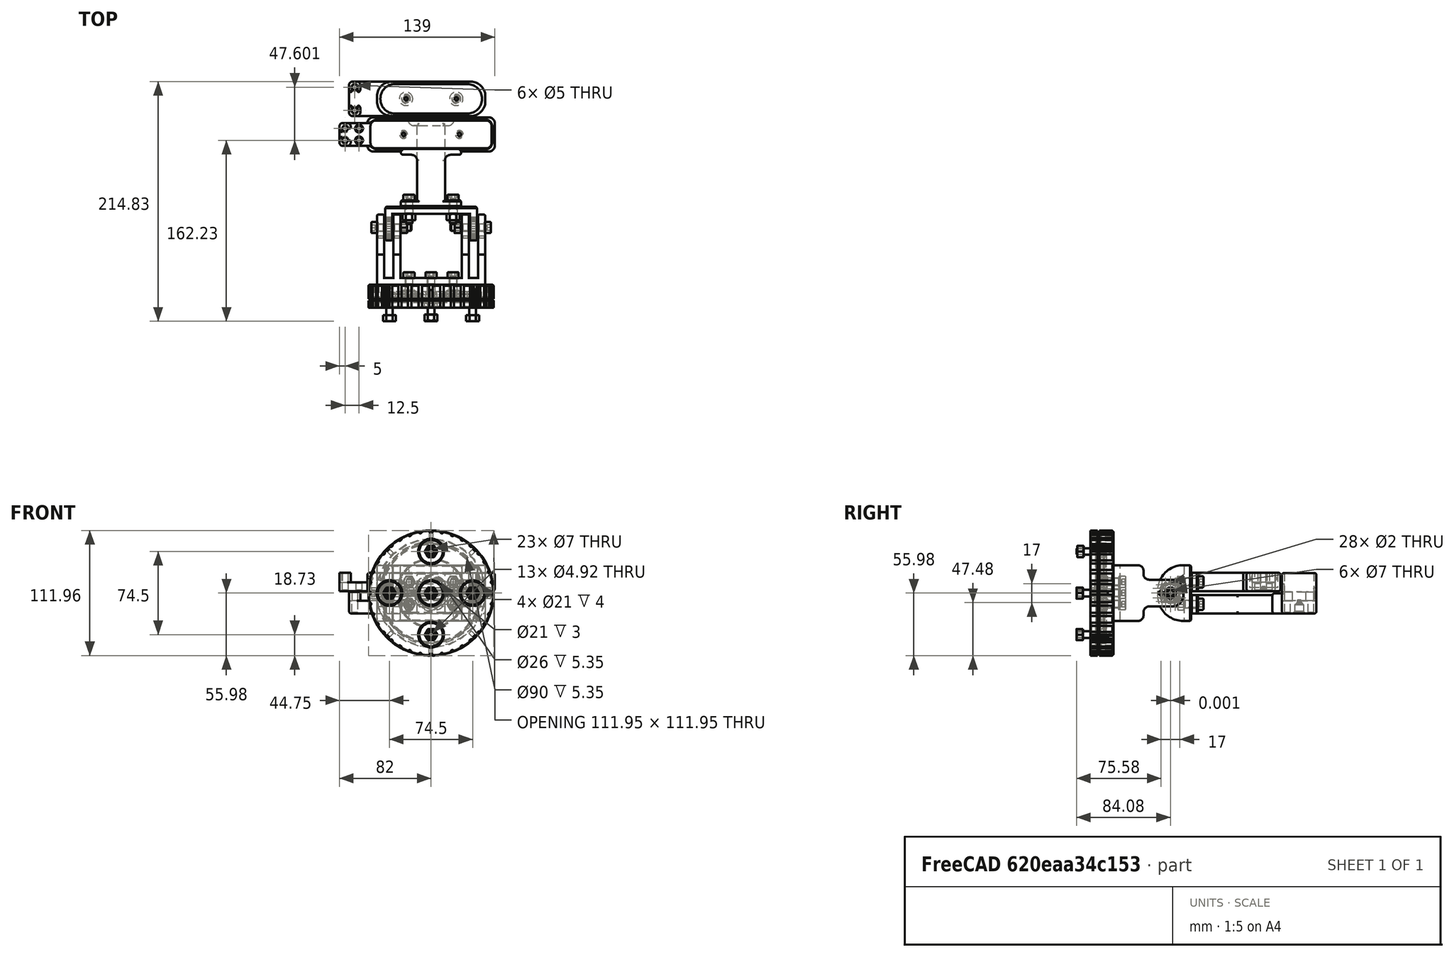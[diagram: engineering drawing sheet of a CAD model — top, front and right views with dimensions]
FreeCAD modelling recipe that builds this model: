
FCSTD DOCUMENT  (FreeCAD 0.18R15576 (Git))
Label: T265_D435i_Fixture
License: All rights reserved
LicenseURL: http://en.wikipedia.org/wiki/All_rights_reserved
objects: Part::FeaturePython×34, Part::Feature×6, App::DocumentObjectGroup×1
note: 40 computed .brp shape members not serialized (recipe doc carries the construction recipe); baked Part::Feature solids carry a one-line shape summary decoded from their .brp

FEATURE [Part::Feature] Chamfer003001002001003001001  label="az_top"
  Placement = pos=(0,-9,0) rot=(0,0,1;0rad)
  shape: bbox 112 x 12.7 x 116.8 mm, 171 faces (baked)
FEATURE [Part::Feature] Chamfer003001002001003001002004001002001001  label="az_bottom"
  Placement = pos=(0,-10,0) rot=(0,0,1;0rad)
  shape: bbox 112 x 14.62 x 116.8 mm, 201 faces (baked)
FEATURE [Part::Feature] Chamfer003001002001003001002004001002001002001  label="el_bottom"
  Placement = pos=(0,-3,0) rot=(0,0,1;0rad)
  shape: bbox 96.9 x 63.75 x 50.82 mm, 209 faces (baked)
FEATURE [Part::Feature] Chamfer003001002001003001002004001002001002002001  label="el_top"
  Placement = pos=(0,-6,0) rot=(0,0,1;0rad)
  shape: bbox 82.2 x 31.9 x 53.79 mm, 132 faces (baked)
FEATURE [Part::Feature] Chamfer003001002001003001002004001002001002002002001001  label="t265_fixture"
  shape: bbox 139.4 x 80.91 x 16.5 mm, 152 faces (baked)
FEATURE [Part::Feature] Chamfer003001002001003001002004001002001002002002001002001  label="d435i_fixture"
  shape: bbox 123.1 x 113.7 x 36.3 mm, 188 faces (baked)
FEATURE [Part::FeaturePython] Screw  label="M6x30-Screw001"  # Fasteners workbench fastener (typed FeaturePython)
  Placement = pos=(39.35,-83.399,-26.6996) rot=(0,1,0;1.5708rad)
  baseObject = -> Chamfer003001002001003001002004001002001002001 [Edge176]
  diameter = 7
  invert = true
  length = 7
  matchOuter = false
  offset = 0
  thread = false
  type = 15
FEATURE [Part::FeaturePython] Screw001  label="M6x30-Screw"  # Fasteners workbench fastener (typed FeaturePython)
  Placement = pos=(-55.55,-83.399,-26.6996) rot=(0,-1,0;1.5708rad)
  baseObject = -> Chamfer003001002001003001002004001002001002001 [Edge150]
  diameter = 7
  invert = false
  length = 7
  matchOuter = false
  offset = 0
  thread = false
  type = 15
FEATURE [Part::FeaturePython] Nut001  label="M6-Nut003"  # Fasteners workbench fastener (typed FeaturePython)
  Placement = pos=(-29.55,-83.399,-26.6996) rot=(0,-1,0;1.5708rad)
  baseObject = -> Screw001 [Edge16]
  diameter = 2
  invert = false
  matchOuter = false
  offset = 4
  thread = false
  type = 5
FEATURE [Part::FeaturePython] Screw002  label="M6x20-Screw"  # Fasteners workbench fastener (typed FeaturePython)
  Placement = pos=(11.65,-59.9,-36.7) rot=(-1,0,0;1.5708rad)
  baseObject = -> Chamfer003001002001003001002004001002001002002002001002001 [Edge302]
  diameter = 7
  invert = false
  length = 5
  matchOuter = false
  offset = 0
  thread = false
  type = 15
FEATURE [Part::FeaturePython] Nut002  label="M6-Nut002"  # Fasteners workbench fastener (typed FeaturePython)
  Placement = pos=(11.65,-76.9,-36.7) rot=(-1,0,0;1.5708rad)
  baseObject = -> Screw002 [Edge14]
  diameter = 2
  invert = false
  matchOuter = false
  offset = 3
  thread = false
  type = 5
FEATURE [Part::FeaturePython] Screw003  label="M6x20-Screw001"  # Fasteners workbench fastener (typed FeaturePython)
  Placement = pos=(-27.85,-59.9,-36.7) rot=(-1,0,0;1.5708rad)
  baseObject = -> Chamfer003001002001003001002004001002001002002002001002001 [Edge63]
  diameter = 7
  invert = false
  length = 5
  matchOuter = false
  offset = 0
  thread = false
  type = 15
FEATURE [Part::FeaturePython] Screw004  label="M6x20-Screw002"  # Fasteners workbench fastener (typed FeaturePython)
  Placement = pos=(11.65,-59.9,-16.7) rot=(-1,0,0;1.5708rad)
  baseObject = -> Chamfer003001002001003001002004001002001002002002001001 [Edge268]
  diameter = 7
  invert = false
  length = 5
  matchOuter = false
  offset = 0
  thread = false
  type = 15
FEATURE [Part::FeaturePython] Screw005  label="M6x20-Screw003"  # Fasteners workbench fastener (typed FeaturePython)
  Placement = pos=(-27.85,-59.9,-16.7) rot=(-1,0,0;1.5708rad)
  baseObject = -> Chamfer003001002001003001002004001002001002002002001001 [Edge288]
  diameter = 7
  invert = false
  length = 5
  matchOuter = false
  offset = 0
  thread = false
  type = 15
FEATURE [Part::FeaturePython] Nut003  label="M6-Nut004"  # Fasteners workbench fastener (typed FeaturePython)
  Placement = pos=(-27.85,-76.9,-16.7) rot=(-1,0,0;1.5708rad)
  baseObject = -> Screw005 [Edge14]
  diameter = 2
  invert = false
  matchOuter = false
  offset = 3
  thread = false
  type = 5
FEATURE [Part::FeaturePython] Nut004  label="M6-Nut005"  # Fasteners workbench fastener (typed FeaturePython)
  Placement = pos=(11.65,-76.9,-16.7) rot=(-1,0,0;1.5708rad)
  baseObject = -> Screw004 [Edge14]
  diameter = 2
  invert = false
  matchOuter = false
  offset = 3
  thread = false
  type = 5
FEATURE [Part::FeaturePython] Nut005  label="M6-Nut006"  # Fasteners workbench fastener (typed FeaturePython)
  Placement = pos=(-27.85,-76.9,-36.7) rot=(-1,0,0;1.5708rad)
  baseObject = -> Screw003 [Edge14]
  diameter = 2
  invert = false
  matchOuter = false
  offset = 3
  thread = false
  type = 5
FEATURE [Part::FeaturePython] Screw006  label="M6x16-Screw"  # Fasteners workbench fastener (typed FeaturePython)
  Placement = pos=(11.65,-129.48,-16.7) rot=(-1,0,0;1.5708rad)
  baseObject = -> Chamfer003001002001003001002004001002001002001 [Edge226]
  diameter = 7
  invert = true
  length = 4
  matchOuter = false
  offset = 0
  thread = false
  type = 15
FEATURE [Part::FeaturePython] Nut006  label="M6-Nut007"  # Fasteners workbench fastener (typed FeaturePython)
  Placement = pos=(11.65,-145.48,-16.7) rot=(-1,0,0;1.5708rad)
  baseObject = -> Screw006 [Edge14]
  diameter = 2
  invert = false
  matchOuter = false
  offset = 0
  thread = false
  type = 5
FEATURE [Part::FeaturePython] Screw007  label="M6x16-Screw001"  # Fasteners workbench fastener (typed FeaturePython)
  Placement = pos=(11.65,-129.48,-36.7) rot=(-1,0,0;1.5708rad)
  baseObject = -> Chamfer003001002001003001002004001002001002001 [Edge97]
  diameter = 7
  invert = true
  length = 4
  matchOuter = false
  offset = 0
  thread = false
  type = 15
FEATURE [Part::FeaturePython] Screw008  label="M6x16-Screw003"  # Fasteners workbench fastener (typed FeaturePython)
  Placement = pos=(-27.85,-129.48,-16.7) rot=(-1,0,0;1.5708rad)
  baseObject = -> Chamfer003001002001003001002004001002001002001 [Edge230]
  diameter = 7
  invert = true
  length = 4
  matchOuter = false
  offset = 0
  thread = false
  type = 15
FEATURE [Part::FeaturePython] Screw009  label="M6x16-Screw002"  # Fasteners workbench fastener (typed FeaturePython)
  Placement = pos=(-27.85,-129.48,-36.7) rot=(-1,0,0;1.5708rad)
  baseObject = -> Chamfer003001002001003001002004001002001002001 [Edge228]
  diameter = 7
  invert = true
  length = 4
  matchOuter = false
  offset = 0
  thread = false
  type = 15
FEATURE [Part::FeaturePython] Nut007  label="M6-Nut008"  # Fasteners workbench fastener (typed FeaturePython)
  Placement = pos=(11.65,-145.48,-36.7) rot=(-1,0,0;1.5708rad)
  baseObject = -> Screw007 [Edge14]
  diameter = 2
  invert = false
  matchOuter = false
  offset = 0
  thread = false
  type = 5
FEATURE [Part::FeaturePython] Nut008  label="M6-Nut009"  # Fasteners workbench fastener (typed FeaturePython)
  Placement = pos=(-27.85,-145.48,-36.7) rot=(-1,0,0;1.5708rad)
  baseObject = -> Screw009 [Edge14]
  diameter = 2
  invert = false
  matchOuter = false
  offset = 0
  thread = false
  type = 5
FEATURE [Part::FeaturePython] Nut009  label="M6-Nut010"  # Fasteners workbench fastener (typed FeaturePython)
  Placement = pos=(-27.85,-145.48,-16.7) rot=(-1,0,0;1.5708rad)
  baseObject = -> Screw008 [Edge14]
  diameter = 2
  invert = false
  matchOuter = false
  offset = 0
  thread = false
  type = 5
FEATURE [Part::FeaturePython] Screw010  label="M6x25-Screw"  # Fasteners workbench fastener (typed FeaturePython)
  Placement = pos=(-8.10005,-129.48,-26.7) rot=(-1,0,0;1.5708rad)
  baseObject = -> Chamfer003001002001003001002004001002001002001 [Edge224]
  diameter = 7
  invert = true
  length = 6
  matchOuter = false
  offset = 0
  thread = false
  type = 15
FEATURE [Part::FeaturePython] Nut  label="M6-Nut"  # Fasteners workbench fastener (typed FeaturePython)
  Placement = pos=(12.9634,-83.399,-26.6996) rot=(0,1,0;1.5708rad)
  baseObject = -> Screw [Edge14]
  diameter = 2
  invert = false
  matchOuter = false
  offset = 3
  thread = false
  type = 5
FEATURE [Part::FeaturePython] Nut010  label="M6-Nut011"  # Fasteners workbench fastener (typed FeaturePython)
  Placement = pos=(-8.10005,-154.48,-26.7) rot=(-1,0,0;1.5708rad)
  baseObject = -> Screw010 [Edge14]
  diameter = 8
  invert = false
  matchOuter = false
  offset = 0
  thread = false
  type = 6
FEATURE [Part::FeaturePython] Screw011  label="M6x20-Screw006"  # Fasteners workbench fastener (typed FeaturePython)
  Placement = pos=(-8.09989,-147.48,-63.95) rot=(-1,0,0;1.5708rad)
  baseObject = -> Chamfer003001002001003001002004001002001001 [Edge349]
  diameter = 7
  invert = false
  length = 5
  matchOuter = false
  offset = 0
  thread = false
  type = 15
FEATURE [Part::FeaturePython] Screw012  label="M6x20-Screw007"  # Fasteners workbench fastener (typed FeaturePython)
  Placement = pos=(-45.35,-147.48,-26.7002) rot=(-1,0,0;1.5708rad)
  baseObject = -> Chamfer003001002001003001002004001002001001 [Edge355]
  diameter = 7
  invert = false
  length = 5
  matchOuter = false
  offset = 0
  thread = false
  type = 15
FEATURE [Part::FeaturePython] Screw013  label="M6x20-Screw004"  # Fasteners workbench fastener (typed FeaturePython)
  Placement = pos=(-8.1002,-147.48,10.55) rot=(-1,0,0;1.5708rad)
  baseObject = -> Chamfer003001002001003001002004001002001001 [Edge353]
  diameter = 7
  invert = false
  length = 5
  matchOuter = false
  offset = 0
  thread = false
  type = 15
FEATURE [Part::FeaturePython] Screw014  label="M6x20-Screw005"  # Fasteners workbench fastener (typed FeaturePython)
  Placement = pos=(29.15,-147.48,-26.6998) rot=(-1,0,0;1.5708rad)
  baseObject = -> Chamfer003001002001003001002004001002001001 [Edge351]
  diameter = 7
  invert = false
  length = 5
  matchOuter = false
  offset = 0
  thread = false
  type = 15
FEATURE [Part::FeaturePython] Nut011  label="M6-Nut017"  # Fasteners workbench fastener (typed FeaturePython)
  Placement = pos=(-45.35,-167.48,-26.7002) rot=(-1,0,0;1.5708rad)
  baseObject = -> Screw012 [Edge14]
  diameter = 2
  invert = false
  matchOuter = false
  offset = 0
  thread = false
  type = 5
FEATURE [Part::FeaturePython] Nut012  label="M6-Nut016"  # Fasteners workbench fastener (typed FeaturePython)
  Placement = pos=(-8.09989,-167.48,-63.95) rot=(-1,0,0;1.5708rad)
  baseObject = -> Screw011 [Edge14]
  diameter = 2
  invert = false
  matchOuter = false
  offset = 0
  thread = false
  type = 5
FEATURE [Part::FeaturePython] Nut013  label="M6-Nut015"  # Fasteners workbench fastener (typed FeaturePython)
  Placement = pos=(29.15,-167.48,-26.6998) rot=(-1,0,0;1.5708rad)
  baseObject = -> Screw014 [Edge14]
  diameter = 2
  invert = false
  matchOuter = false
  offset = 0
  thread = false
  type = 5
FEATURE [Part::FeaturePython] Nut014  label="M6-Nut018"  # Fasteners workbench fastener (typed FeaturePython)
  Placement = pos=(-8.1002,-166.867,10.55) rot=(-1,0,0;1.5708rad)
  baseObject = -> Screw013 [Edge12]
  diameter = 2
  invert = false
  matchOuter = false
  offset = 0
  thread = false
  type = 5
FEATURE [Part::FeaturePython] Screw016  label="M3x4-Screw"  # Fasteners workbench fastener (typed FeaturePython)
  Placement = pos=(-30.5,31.9,-36.95) rot=(1,0,0;3.14159rad)
  baseObject = -> Chamfer003001002001003001002004001002001002002002001002001 [Edge439]
  diameter = 4
  invert = false
  length = 0
  matchOuter = false
  offset = 0
  thread = false
  type = 17
FEATURE [Part::FeaturePython] Screw017  label="M3x4-Screw001"  # Fasteners workbench fastener (typed FeaturePython)
  Placement = pos=(14.5,31.9,-36.95) rot=(1,0,0;3.14159rad)
  baseObject = -> Chamfer003001002001003001002004001002001002002002001002001 [Edge440]
  diameter = 4
  invert = false
  length = 0
  matchOuter = false
  offset = 0
  thread = false
  type = 17
FEATURE [Part::FeaturePython] Screw019  label="M3x4-Screw002"  # Fasteners workbench fastener (typed FeaturePython)
  Placement = pos=(-32.75,0,-24.95) rot=(1,0,0;3.14159rad)
  baseObject = -> Chamfer003001002001003001002004001002001002002002001001 [Edge31]
  diameter = 4
  invert = false
  length = 0
  matchOuter = false
  offset = 0
  thread = false
  type = 17
FEATURE [Part::FeaturePython] Screw021  label="M3x4-Screw003"  # Fasteners workbench fastener (typed FeaturePython)
  Placement = pos=(17.25,0,-24.95) rot=(1,0,0;3.14159rad)
  baseObject = -> Chamfer003001002001003001002004001002001002002002001001 [Edge30]
  diameter = 4
  invert = false
  length = 0
  matchOuter = false
  offset = 0
  thread = false
  type = 17
FEATURE [App::DocumentObjectGroup] Group001  label="fasteners"
  Group = -> [Screw009,Nut007,Nut008,Nut009,Screw010,Nut005,Screw006,Nut006,Screw007,Screw008,Screw003,Screw004,Screw005,Nut003,Nut004,Screw001,Nut001,Screw002,Nut002,Screw,Nut,Nut010,Screw011,Screw012,Screw013,Screw014,Nut011,Nut012,Nut013,Nut014,Screw016,Screw017,Screw019,Screw021]
